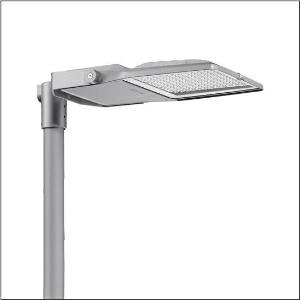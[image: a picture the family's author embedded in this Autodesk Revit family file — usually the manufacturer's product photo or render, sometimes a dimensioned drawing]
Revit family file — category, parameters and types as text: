
# Revit family: floodlight_fl_21_iq_midi___pl61_5xa7782f4c3a_0871
name_source: partatom
category: Lighting Fixtures
units: mm (PartAtom-declared; Revit-internal decimal feet)

## family parameters
Cut with Voids When Loaded = No
Host = Face
Light Source = No
Part Type = Normal
Room Calculation Point = No
Round Connector Dimension = Use Diameter
Shared = No

## types (1)
- --- (1 x LED, 36650 lm, 270.2 W, 4000K)
    Apparent Load = 270 VA
    CIE Flux Codes = 33 65 98 100 100
    Color Rendering = 70
    Color Temperature = 4000K
    Default Elevation = 1800 mm
    Description = Floodlight FL 21 iQ midi, floodlight, primary light control with lens, of PMMA, primary optical cover: protective disc, of toughened safety glass, transparent, light distribution: PL61, light emission: direct distribution, installation type: surface-mounted, LED, High Power LED, rated luminous flux: 36.650lm, luminous efficacy: 136lm/W, light colour: 740, colour temperature: 4000K, control gear: ECG iQ, control: optimised constant luminous flux control (CLO 2.0), Desk-Remote (wireless, voltage-free reading and setting of iQ features in the workshop via application-optimized NFC function/RFID function), Smart-Wire, Night-Set, Temp-Guard, Auto-Match, Street-Remote, with terminal, 6-pole, mains connection: 220..240V, AC, 50/60Hz, start of lifetime: 270W, end of service life: 287W, reduction: 118W, luminaire housing, of diecast aluminium, powder-coated, Siteco® metallic grey (DB 702S), corrosivity category C5 mid according to DIN EN ISO 12944, sealing non-destructively replaceable, please order mast flange separately, mast bracket, of steel, galvanised, powder-coated, Siteco® metallic grey (DB 702S), protection rating (complete): IP66, insulation class (complete): insulation class II (safety insulation), certification: CE, protection symbol: D, impact resistance: IK08, permissible operating ambient temperature: -40..+40°C, permissible operating ambient temperature for outdoor applications: -40..+50°C, standard: DIN EN 12944, LABS conformity tested according to VDMA 24364:2018-05, packaging unit: 1 piece

Light Distribution: PL61
    Height = 76 mm
    Lamp = 1 x LED
    Lamp Light Flux = 36650 lm
    Lamp Power = 270.2 W
    Lamp count = 1
    Length = 657 mm
    Luminous efficacy = 136 lm/W
    Manufacturer = Siteco
    ModVariant = No
    Model = 5XA7782F4C3A
    Number of Poles = 1
    OnlyDefault = Yes
    Power Factor = 1
    Product Name = Floodlight FL 21 iQ midi | PL61
    Product group = floodlight | pylon annexe
    ProductGroupID = 6200
    Protection Class = Protection class II
    Protection Degree = IP 66
    RLX_Detail_Level = 1
    RLX_Emergency_Light_Flux = 0 lm
    RLX_Emergency_Type = 0
    RLX_Emergency_Type_DB = No
    RlxData = <blob elided: 153813 chars, md5=479094a6>
    Socket = socket
    Standby Power = 0 W
    System Light Flux = 36650 lm
    System Power = 270 W
    Type Comments = factory setting: luminous flux: 100 % | dim-lin: 254 | 620 mA
    Type Image = l_1007123.jpg
    URL = http://relux.com
    VarID = @adj_038311
    Voltage = 0 V
    Weight = 0.00 kg
    Width = 442 mm

## geometry (parser evidence)
native form markers: Blend x4, Sweep x12
no freeform markers — native parametric forms only
